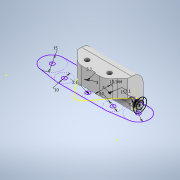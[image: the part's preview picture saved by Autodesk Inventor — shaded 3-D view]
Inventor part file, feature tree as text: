
AUTODESK INVENTOR PART (.ipt)
format: ipt  version: 2020 (Build 240168000, 168)  size: 283,136 bytes
history: native  units: in
note: dims shown in document units (in); Inventor stores cm internally (conversion verified against a paired STEP export)
features: extrude x10, sketch x9, fillet x4, projected_geometry x2
ambient origin geometry x8: Origin, YZ Plane, XZ Plane, XY Plane, X Axis, Y Axis, Z Axis, Center Point
bodies: Solid1 (feature_tree)
feature tree (25):
  sketch  "Sketch1"  dims[d0=0.3937in d1=0.3937in d2=0.5906in d3=0.5906in d4=0.122in d5=0.122in d6=0.122in d7=0.2362in d8=0.0in]
  sketch  "Sketch2"  dims[d9=0.3346in d10=0.0in d11=0.2953in]
  sketch  "Sketch3"  dims[d12=0.2756in d13=0.0in d15=0.2346in d16=0.1543in]
  extrude  "Extrusion1"  Depth=0.3937in TaperAngle=0.0deg
  extrude  "Extrusion2"  Depth=0.2953in
  extrude  "Extrusion3"  Depth=0.2346in
  sketch  "Sketch6"  dims[d23=0.3346in d24=0.0in d25=0.1181in]
  fillet  "Fillet2"  Radius=0.1543in
  extrude  "Extrusion4"  Depth=0.3543in
  extrude  "Extrusion5"  Depth=0.0394in
  fillet  "Fillet3"  Radius=0.3346in
  extrude  "Extrusion6"  Depth=0.1181in
  extrude  "Extrusion7"  Depth=0.315in TaperAngle=0.0deg
  fillet  "Fillet4"  Radius=0.315in
  extrude  "Extrusion8"  Depth=1.378in
  extrude  "Extrusion9"  Depth=0.315in
  fillet  "Fillet5"  Radius=0.1181in
  extrude  "Extrusion10"  Depth=0.1181in
  sketch  "Sketch4"  dims[d17=0.2008in d18=0.3543in]
  projected_geometry  "Projected Loop1"
  sketch  "Sketch5"  dims[d19=0.0394in d20=0.0394in d21=0.3346in d22=0.0in]
  sketch  "Sketch7"  dims[d26=0.3346in d27=0.0in d28=0.2362in d29=0.0in d30=0.315in]
  projected_geometry  "Projected Loop2"
  sketch  "Sketch8"  dims[d32=0.0in d33=0.0in d34=1.378in]
  sketch  "Sketch9"  dims[d35=0.2362in d36=0.0in d37=0.315in d38=0.1181in d39=0.1181in d40=0.2362in d41=0.0in d42=0.4151in]
